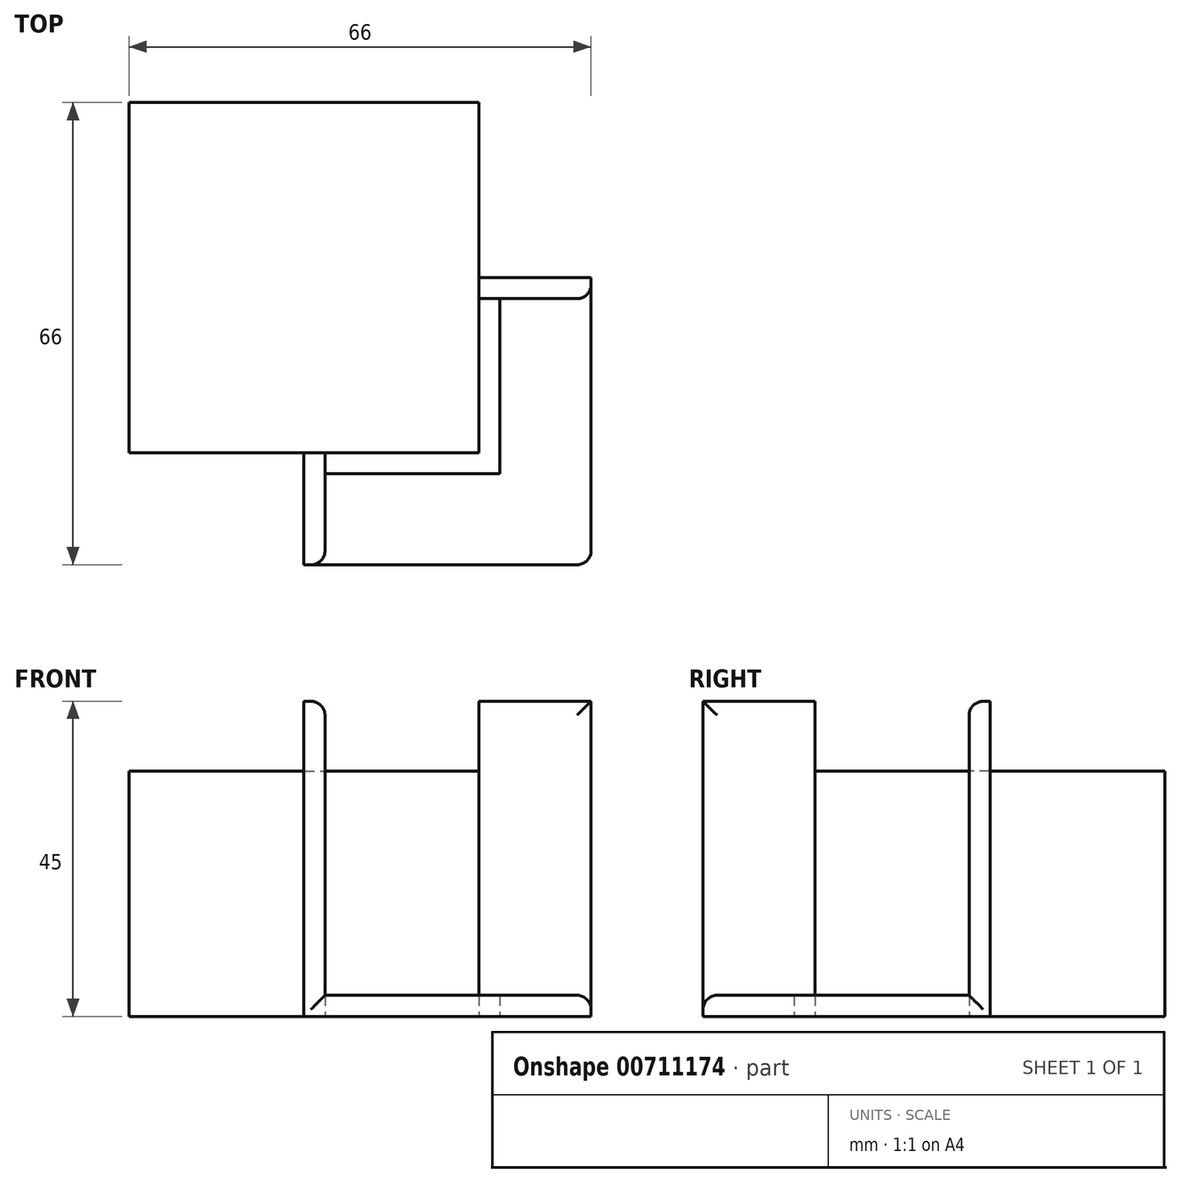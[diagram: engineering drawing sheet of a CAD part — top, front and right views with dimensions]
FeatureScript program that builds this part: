
annotation { "Feature Type Name" : "Feature", "Feature Type Description" : "" }
export const myFeature = defineFeature(function(context is Context, id is Id, definition is map)
    precondition{}
    {
        {
            var Q0;
            Q0=qCreatedBy(makeId("Top.planeOp"),FACE);
            var sketch = newSketch(context, id + "F0", { "sketchPlane" : qUnion([Q0])});
            skLineSegment(sketch, "E0.bottom", {"start": v(0, 0) * mm, "end": v(50, 0) * mm});
            skLineSegment(sketch, "E0.top", {"start": v(0, -50) * mm, "end": v(50, -50) * mm});
            skLineSegment(sketch, "E0.left", {"start": v(0, 0) * mm, "end": v(0, -50) * mm});
            skLineSegment(sketch, "E0.right", {"start": v(50, 0) * mm, "end": v(50, -50) * mm});
            skLineSegment(sketch, "E1", {"start": v(25, -50) * mm, "end": v(25, -66) * mm});
            skLineSegment(sketch, "E2", {"start": v(50, -25) * mm, "end": v(66, -25) * mm});
            skLineSegment(sketch, "E3", {"start": v(66, -25) * mm, "end": v(66, -66) * mm});
            skLineSegment(sketch, "E4", {"start": v(66, -66) * mm, "end": v(25, -66) * mm});
            skLineSegment(sketch, "E5", {"start": v(50, -25) * mm, "end": v(50, -28) * mm});
            skLineSegment(sketch, "E6", {"start": v(50, -28) * mm, "end": v(66, -28) * mm});
            skLineSegment(sketch, "E7", {"start": v(25, -50) * mm, "end": v(28, -50) * mm});
            skLineSegment(sketch, "E8", {"start": v(28, -50) * mm, "end": v(28, -66) * mm});
            skLineSegment(sketch, "E9", {"start": v(28, -53) * mm, "end": v(28, -50) * mm});
            skLineSegment(sketch, "E10", {"start": v(50, -28) * mm, "end": v(53, -28) * mm});
            skLineSegment(sketch, "E11", {"start": v(53, -28) * mm, "end": v(53, -53) * mm});
            skLineSegment(sketch, "E12", {"start": v(53, -53) * mm, "end": v(28, -53) * mm});
            skSolve(sketch);
        }
        {
            var Q0;
            {var subQ6=sQuery(id+"F0.wireOp",EDGE,"E0.bottom");Q0=makeQuery(id+"F0.imprint","IMPRINT",FACE,{"disambiguationData":[TD([[makeQuery(id+"F0.imprint","IMPRINT",EDGE,{"derivedFrom":subQ6}),-1.0]])]});}
            extrude(context, id + "F1", {"entities" : qUnion([Q0]), "depth" : 35 * mm, "offsetDistance" : 25 * mm});
        }
        {
            var Q0;
            {var subQ2=sQuery(id+"F0.wireOp",EDGE,"E1");Q0=makeQuery(id+"F0.imprint","IMPRINT",FACE,{"disambiguationData":[TD([[makeQuery(id+"F0.imprint","IMPRINT",EDGE,{"derivedFrom":subQ2}),1.0]])]});}
            var Q1;
            {var subQ2=sQuery(id+"F0.wireOp",EDGE,"E2");Q1=makeQuery(id+"F0.imprint","IMPRINT",FACE,{"disambiguationData":[TD([[makeQuery(id+"F0.imprint","IMPRINT",EDGE,{"derivedFrom":subQ2}),-1.0]])]});}
            var Q2;
            {var subQ0=sQuery(id+"F0.wireOp",EDGE,"E9");Q2=makeQuery(id+"F0.imprint","IMPRINT",FACE,{"disambiguationData":[TD([[makeQuery(id+"F0.imprint","IMPRINT",EDGE,{"derivedFrom":subQ0}),-1.0]])]});}
            extrude(context, id + "F2", {"entities" : qUnion([Q0, Q1, Q2]), "operationType" : NewBodyOperationType.ADD, "depth" : 45 * mm, "offsetDistance" : 25 * mm});
        }
        {
            var Q0;
            Q0 = qSketchRegion(id + "F0", true);
            extrude(context, id + "F3", {"entities" : qUnion([Q0]), "operationType" : NewBodyOperationType.ADD, "depth" : 3 * mm, "offsetDistance" : 25 * mm});
        }
        {
            var Q0;
            Q0=makeQuery(id+"F3.opExtrude","CAP_EDGE",EDGE,{"disambiguationData":[OSD([sQuery(id+"F0.wireOp",EDGE,"E4")])],"isStart":false});
            var Q1;
            Q1=makeQuery(id+"F3.opExtrude","CAP_EDGE",EDGE,{"disambiguationData":[OSD([sQuery(id+"F0.wireOp",EDGE,"E3")])],"isStart":false});
            var Q2;
            Q2=makeQuery(id+"F3.opExtrude","SWEPT_EDGE",EDGE,{"disambiguationData":[OSD([sQuery(id+"F0.wireOp",EDGE,"E3"),sQuery(id+"F0.wireOp",EDGE,"E4")])]});
            var Q3;
            Q3=makeQuery(id+"F2.opExtrude","SWEPT_EDGE",EDGE,{"disambiguationData":[OSD([sQuery(id+"F0.wireOp",EDGE,"E11"),sQuery(id+"F0.wireOp",EDGE,"E12")])]});
            var Q4;
            Q4=makeQuery(id+"F2.opExtrude","CAP_EDGE",EDGE,{"disambiguationData":[OSD([sQuery(id+"F0.wireOp",EDGE,"E12")])],"isStart":false});
            var Q5;
            Q5=makeQuery(id+"F2.opExtrude","CAP_EDGE",EDGE,{"disambiguationData":[OSD([sQuery(id+"F0.wireOp",EDGE,"E8")])],"isStart":false});
            var Q6;
            Q6=makeQuery(id+"F2.opExtrude","CAP_EDGE",EDGE,{"disambiguationData":[OSD([sQuery(id+"F0.wireOp",EDGE,"E11")])],"isStart":false});
            var Q7;
            Q7=makeQuery(id+"F2.opExtrude","CAP_EDGE",EDGE,{"disambiguationData":[OSD([sQuery(id+"F0.wireOp",EDGE,"E6")])],"isStart":false});
            var Q8;
            Q8=makeQuery(id+"F2.opExtrude","SWEPT_EDGE",EDGE,{"disambiguationData":[OSD([sQuery(id+"F0.wireOp",EDGE,"E3"),sQuery(id+"F0.wireOp",EDGE,"E6")])]});
            var Q9;
            Q9=makeQuery(id+"F2.opExtrude","SWEPT_EDGE",EDGE,{"disambiguationData":[OSD([sQuery(id+"F0.wireOp",EDGE,"E4"),sQuery(id+"F0.wireOp",EDGE,"E8")])]});
            fillet(context, id + "F4", {"entities" : qUnion([Q0, Q1, Q2, Q3, Q4, Q5, Q6, Q7, Q8, Q9]), "radius" : 2 * mm, "tangentPropagation" : true, "allowEdgeOverflow" : false});
        }
    });
